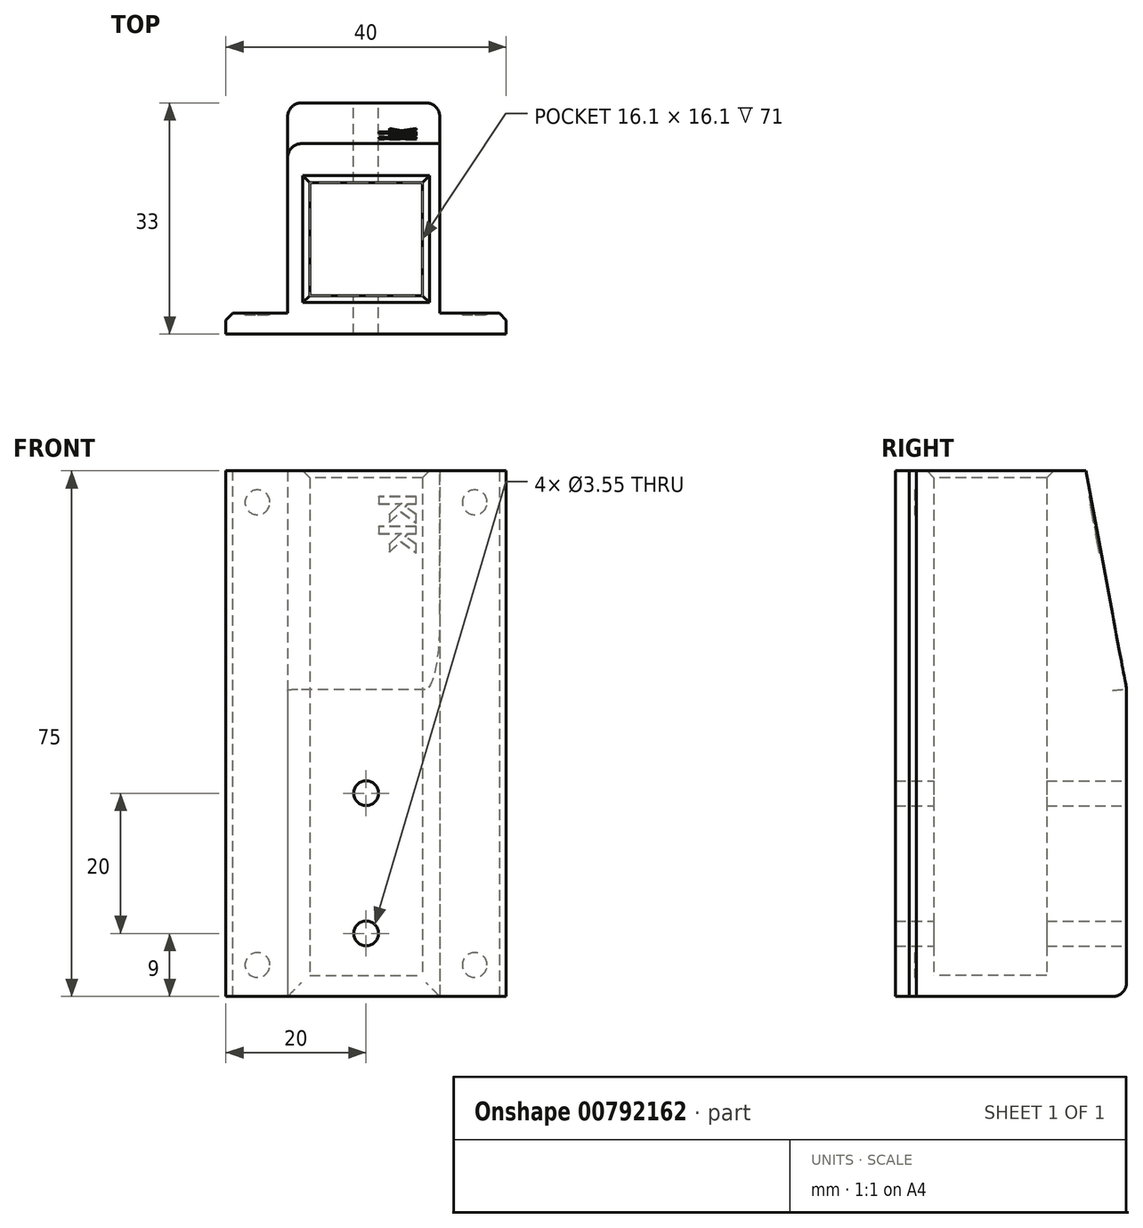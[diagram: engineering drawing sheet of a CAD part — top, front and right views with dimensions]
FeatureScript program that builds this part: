
annotation { "Feature Type Name" : "Feature", "Feature Type Description" : "" }
export const myFeature = defineFeature(function(context is Context, id is Id, definition is map)
    precondition{}
    {
        {
            var Q0;
            Q0=qCreatedBy(makeId("Top.planeOp"),FACE);
            var sketch = newSketch(context, id + "F0", { "sketchPlane" : qUnion([Q0])});
            skLineSegment(sketch, "E0.bottom", {"start": v(-8.05, 8.05) * mm, "end": v(8.05, 8.05) * mm});
            skLineSegment(sketch, "E0.top", {"start": v(-8.05, -8.05) * mm, "end": v(8.05, -8.05) * mm});
            skLineSegment(sketch, "E0.left", {"start": v(-8.05, 8.05) * mm, "end": v(-8.05, -8.05) * mm});
            skLineSegment(sketch, "E0.right", {"start": v(8.05, 8.05) * mm, "end": v(8.05, -8.05) * mm});
            skPoint(sketch, "E0.middle", {"position": v(0, 0) * mm});
            skLineSegment(sketch, "E1.bottom", {"start": v(-11.2, -10.55) * mm, "end": v(10.52, -10.55) * mm});
            skLineSegment(sketch, "E1.top", {"start": v(-11.2, 19.45) * mm, "end": v(10.52, 19.45) * mm});
            skLineSegment(sketch, "E1.left", {"start": v(-11.2, -10.55) * mm, "end": v(-11.2, 19.45) * mm});
            skLineSegment(sketch, "E1.right", {"start": v(10.52, -10.55) * mm, "end": v(10.52, 19.45) * mm});
            skLineSegment(sketch, "E2.bottom", {"start": v(-20, -13.55) * mm, "end": v(20, -13.55) * mm});
            skLineSegment(sketch, "E2.top", {"start": v(-20, -10.55) * mm, "end": v(20, -10.55) * mm});
            skLineSegment(sketch, "E2.left", {"start": v(-20, -13.55) * mm, "end": v(-20, -10.55) * mm});
            skLineSegment(sketch, "E2.right", {"start": v(20, -13.55) * mm, "end": v(20, -10.55) * mm});
            skSolve(sketch);
        }
        {
            var Q0;
            Q0 = qSketchRegion(id + "F0", true);
            extrude(context, id + "F1", {"entities" : qUnion([Q0]), "depth" : 75 * mm, "offsetDistance" : 25 * mm});
        }
        {
            var Q0;
            Q0=qCreatedBy(makeId("Right.planeOp"),FACE);
            var sketch = newSketch(context, id + "F2", { "sketchPlane" : qUnion([Q0])});
            skLineSegment(sketch, "E3.bottom", {"start": v(-10, 0) * mm, "end": v(10, 0) * mm});
            skLineSegment(sketch, "E3.top", {"start": v(-10, 3) * mm, "end": v(10, 3) * mm});
            skLineSegment(sketch, "E3.left", {"start": v(-10, 0) * mm, "end": v(-10, 3) * mm});
            skLineSegment(sketch, "E3.right", {"start": v(10, 0) * mm, "end": v(10, 3) * mm});
            skSolve(sketch);
        }
        {
            var Q0;
            Q0 = qSketchRegion(id + "F2", true);
            extrude(context, id + "F3", {"entities" : qUnion([Q0]), "operationType" : NewBodyOperationType.ADD, "depth" : 10 * mm, "offsetDistance" : 25 * mm, "hasSecondDirection" : true, "secondDirectionOppositeDirection" : true, "secondDirectionDepth" : 10 * mm});
        }
        {
            var Q0;
            {var subQ0=sQuery(id+"F0.wireOp",EDGE,"E2.top");Q0=makeQuery(id+"F1.opExtrude","SWEPT_FACE",FACE,{"disambiguationData":[OSD([subQ0]),TDD([makeQuery(id+"F0.imprint","IMPRINT",EDGE,{"disambiguationData":[TD([[makeQuery(id+"F0.imprint","INTERSECT",VERTEX,{"derivedFrom":[sQuery(id+"F0.wireOp",EDGE,"E1.right"),subQ0]}),-1.0]])],"derivedFrom":subQ0})])]});}
            var sketch = newSketch(context, id + "F4", { "sketchPlane" : qUnion([Q0])});
            skCircle(sketch, "E4", {"center": v(-15.5, 4.5) * mm, "radius": 1.77 * mm});
            skCircle(sketch, "E5", {"center": v(15.5, 4.5) * mm, "radius": 1.77 * mm});
            skCircle(sketch, "E6", {"center": v(-15.5, 70.5) * mm, "radius": 1.77 * mm});
            skCircle(sketch, "E7", {"center": v(15.5, 70.5) * mm, "radius": 1.77 * mm});
            skSolve(sketch);
        }
        {
            var Q0;
            Q0 = qSketchRegion(id + "F4", true);
            extrude(context, id + "F5", {"entities" : qUnion([Q0]), "operationType" : NewBodyOperationType.REMOVE, "oppositeDirection" : true, "depth" : .25 * mm, "offsetDistance" : 25 * mm});
        }
        {
            var Q0;
            Q0=makeQuery(id+"F1.opExtrude","SWEPT_FACE",FACE,{"disambiguationData":[OSD([sQuery(id+"F0.wireOp",EDGE,"E1.top")])]});
            var sketch = newSketch(context, id + "F6", { "sketchPlane" : qUnion([Q0])});
            skCircle(sketch, "E8", {"center": v(0, 9) * mm, "radius": 1.77 * mm});
            skCircle(sketch, "E9", {"center": v(0, 29) * mm, "radius": 1.77 * mm});
            skSolve(sketch);
        }
        {
            var Q0;
            Q0 = qSketchRegion(id + "F6", true);
            extrude(context, id + "F7", {"entities" : qUnion([Q0]), "operationType" : NewBodyOperationType.REMOVE, "oppositeDirection" : true, "depth" : 40 * mm, "offsetDistance" : 25 * mm});
        }
        {
            var Q0;
            Q0=makeQuery(id+"F1.opExtrude","CAP_EDGE",EDGE,{"disambiguationData":[OSD([sQuery(id+"F0.wireOp",EDGE,"E0.left")])],"isStart":false});
            var Q1;
            Q1=makeQuery(id+"F1.opExtrude","CAP_EDGE",EDGE,{"disambiguationData":[OSD([sQuery(id+"F0.wireOp",EDGE,"E0.bottom")])],"isStart":false});
            var Q2;
            Q2=makeQuery(id+"F1.opExtrude","CAP_EDGE",EDGE,{"disambiguationData":[OSD([sQuery(id+"F0.wireOp",EDGE,"E0.right")])],"isStart":false});
            var Q3;
            Q3=makeQuery(id+"F1.opExtrude","CAP_EDGE",EDGE,{"disambiguationData":[OSD([sQuery(id+"F0.wireOp",EDGE,"E0.top")])],"isStart":false});
            chamfer(context, id + "F8", {"entities" : qUnion([Q0, Q1, Q2, Q3]), "width" : 1 * mm, "tangentPropagation" : true});
        }
        {
            var Q0;
            Q0=makeQuery(id+"F1.opExtrude","SWEPT_EDGE",EDGE,{"disambiguationData":[OSD([sQuery(id+"F0.wireOp",EDGE,"E2.top"),sQuery(id+"F0.wireOp",EDGE,"E2.right")])]});
            var Q1;
            Q1=makeQuery(id+"F1.opExtrude","SWEPT_EDGE",EDGE,{"disambiguationData":[OSD([sQuery(id+"F0.wireOp",EDGE,"E2.top"),sQuery(id+"F0.wireOp",EDGE,"E2.left")])]});
            chamfer(context, id + "F9", {"entities" : qUnion([Q0, Q1]), "width" : 1 * mm, "tangentPropagation" : true});
        }
        {
            var Q0;
            Q0=makeQuery(id+"F1.opExtrude","SWEPT_FACE",FACE,{"disambiguationData":[OSD([sQuery(id+"F0.wireOp",EDGE,"E1.right")])]});
            var sketch = newSketch(context, id + "F10", { "sketchPlane" : qUnion([Q0])});
            skLineSegment(sketch, "E10", {"start": v(19.45, 43.86) * mm, "end": v(13.62, 75) * mm});
            skLineSegment(sketch, "E11", {"start": v(13.62, 75) * mm, "end": v(19.45, 75) * mm});
            skLineSegment(sketch, "E12", {"start": v(19.45, 75) * mm, "end": v(19.45, 43.86) * mm});
            skSolve(sketch);
        }
        {
            var Q0;
            Q0 = qSketchRegion(id + "F10", true);
            extrude(context, id + "F11", {"entities" : qUnion([Q0]), "operationType" : NewBodyOperationType.REMOVE, "oppositeDirection" : true, "depth" : 45.4 * mm, "offsetDistance" : 25 * mm});
        }
        {
            var Q0;
            Q0=makeQuery(id+"F1.opExtrude","SWEPT_EDGE",EDGE,{"disambiguationData":[OSD([sQuery(id+"F0.wireOp",EDGE,"E1.top"),sQuery(id+"F0.wireOp",EDGE,"E1.right")])]});
            var Q1;
            Q1=makeQuery(id+"F11.boolean.opBoolean","COPY",EDGE,{"derivedFrom":makeQuery(id+"F11.opExtrude","CAP_EDGE",EDGE,{"disambiguationData":[OSD([sQuery(id+"F10.wireOp",EDGE,"E10")])],"isStart":true})});
            var Q2;
            Q2=makeQuery(id+"F11.boolean.opBoolean","COPY",EDGE,{"derivedFrom":makeQuery(id+"F11.opExtrude","SWEPT_EDGE",EDGE,{"disambiguationData":[OSD([sQuery(id+"F0.wireOp",EDGE,"E1.top"),sQuery(id+"F0.wireOp",EDGE,"E1.right"),sQuery(id+"F10.wireOp",EDGE,"E10"),sQuery(id+"F10.wireOp",EDGE,"E12")])]})});
            var Q3;
            Q3=makeQuery(id+"F1.opExtrude","SWEPT_EDGE",EDGE,{"disambiguationData":[OSD([sQuery(id+"F0.wireOp",EDGE,"E1.top"),sQuery(id+"F0.wireOp",EDGE,"E1.left")])]});
            var Q4;
            Q4=makeQuery(id+"F1.opExtrude","CAP_EDGE",EDGE,{"disambiguationData":[OSD([sQuery(id+"F0.wireOp",EDGE,"E1.top")])],"isStart":true});
            var Q5;
            Q5=makeQuery(id+"F11.boolean.opBoolean","INTERSECT",EDGE,{"derivedFrom":[makeQuery(id+"F1.opExtrude","SWEPT_FACE",FACE,{"disambiguationData":[OSD([sQuery(id+"F0.wireOp",EDGE,"E1.left")])]}),makeQuery(id+"F11.opExtrude","SWEPT_FACE",FACE,{"disambiguationData":[OSD([sQuery(id+"F10.wireOp",EDGE,"E10")])]})]});
            var Q6;
            Q6=makeQuery(id+"F11.boolean.opBoolean","COPY",EDGE,{"derivedFrom":makeQuery(id+"F11.opExtrude","SWEPT_EDGE",EDGE,{"disambiguationData":[OSD([sQuery(id+"F0.wireOp",EDGE,"E1.right"),sQuery(id+"F10.wireOp",EDGE,"E10"),sQuery(id+"F10.wireOp",EDGE,"E11")])]})});
            fillet(context, id + "F12", {"entities" : qUnion([Q0, Q1, Q2, Q3, Q4, Q5, Q6]), "radius" : 2 * mm, "tangentPropagation" : true, "allowEdgeOverflow" : false});
        }
        {
            var Q0;
            Q0=makeQuery(id+"F11.boolean.opBoolean","COPY",FACE,{"derivedFrom":makeQuery(id+"F11.opExtrude","SWEPT_FACE",FACE,{"disambiguationData":[OSD([sQuery(id+"F10.wireOp",EDGE,"E10")])]})});
            var sketch = newSketch(context, id + "F13", { "sketchPlane" : qUnion([Q0])});
            skText(sketch, "E13", { "text": "kk", "fontName": "OpenSans-Bold.ttf"});
            const initialGuessF13  = {"E13": [-0.00715, 0.06802, 0, -1, 0.00503]};
            skSetInitialGuess(sketch, initialGuessF13);
            skSolve(sketch);
        }
        {
            var Q0;
            Q0 = qSketchRegion(id + "F13", true);
            extrude(context, id + "F14", {"entities" : qUnion([Q0]), "operationType" : NewBodyOperationType.REMOVE, "oppositeDirection" : true, "depth" : 0.25 * mm, "offsetDistance" : 25 * mm});
        }
    });
